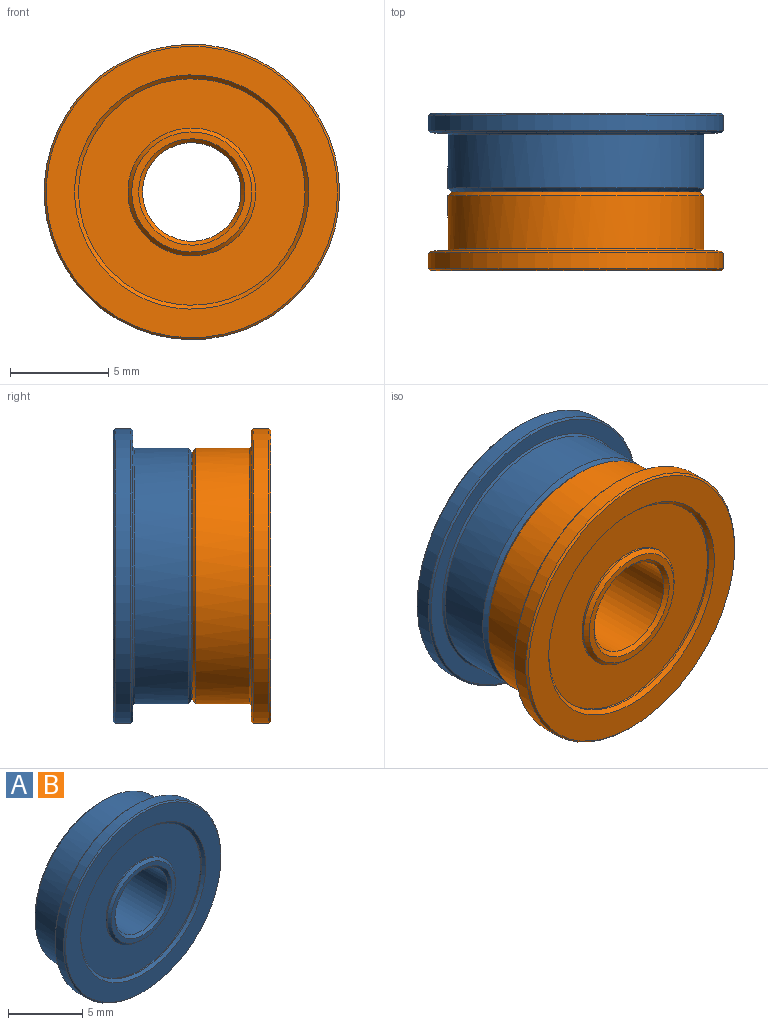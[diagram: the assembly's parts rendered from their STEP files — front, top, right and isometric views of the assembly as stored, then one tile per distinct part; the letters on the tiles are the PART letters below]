
ASSEMBLY  parts=2 mates=1
PART A: 24 faces, bbox 15x4x15 mm
  f0: plane 14.8x14.8mm, normal (0,1,0), area 35.2mm2, adj f1,f23
  f1: cone r=6.55mm half-angle=45deg, axis (0,-1,0), area 5.8mm2, adj f0,f9
  f2: cylinder r=7.5mm len=15mm, axis (0,-1,0), area 37.7mm2, adj f13,f23
  f3: cone r=5.85mm half-angle=45deg, axis (0,1,0), area 10.4mm2, adj f7,f22
  f4: cylinder r=5.75mm len=11.5mm, axis (0,-1,0), area 3.6mm2, adj f11,f18
  f5: cone r=3.15mm half-angle=45deg, axis (0,-1,0), area 5.6mm2, adj f6,f16
  f6: plane 6.1x6.1mm, normal (0,1,0), area 6.3mm2, adj f5,f19
  f7: cylinder r=5.75mm len=11.5mm, axis (0,1,0), area 3.6mm2, adj f3,f17
  f8: cone r=6.4mm half-angle=45deg, axis (0,-1,0), area 11.4mm2, adj f9,f22
  f9: cylinder r=6.5mm len=13mm, axis (0,-1,0), area 110.3mm2, adj f1,f8
  f10: cylinder r=3.25mm len=6.5mm, axis (0,-1,0), area 2mm2, adj f15,f18
  f11: cone r=5.85mm half-angle=45deg, axis (0,-1,0), area 10.4mm2, adj f4,f20
  f12: cone r=2.6mm half-angle=45deg, axis (0,-1,0), area 4.6mm2, adj f14,f21
  f13: cone r=7.45mm half-angle=45deg, axis (0,1,0), area 6.6mm2, adj f2,f20
  f14: cylinder r=2.5mm len=5mm, axis (0,1,0), area 56.5mm2, adj f12,f19
  f15: cone r=3.15mm half-angle=45deg, axis (0,1,0), area 5.6mm2, adj f10,f21
  f16: cylinder r=3.25mm len=6.5mm, axis (0,1,0), area 2mm2, adj f5,f17
  f17: plane 11.5x11.5mm, normal (0,1,0), area 70.7mm2, adj f7,f16
  f18: plane 11.5x11.5mm, normal (0,-1,0), area 70.7mm2, adj f4,f10
  f19: cone r=2.6mm half-angle=45deg, axis (0,1,0), area 4.6mm2, adj f6,f14
  f20: plane 14.8x14.8mm, normal (0,-1,0), area 60.8mm2, adj f11,f13
  f21: plane 6.1x6.1mm, normal (0,-1,0), area 6.3mm2, adj f12,f15
  f22: plane 12.6x12.6mm, normal (0,1,0), area 13.5mm2, adj f3,f8
  f23: cone r=7.45mm half-angle=45deg, axis (0,-1,0), area 6.6mm2, adj f0,f2
PART B: same geometry as A
PLACE A rot(axis=(1,0,0),180deg) t=(-0.56,-4.08,-0.03)mm
PLACE B t=(-0.56,-12.08,-0.03)mm
MATE fastened A.f13 <-> B.f13  axis (0,-1,0) through (-0.56,-8.08,-0.03)mm
